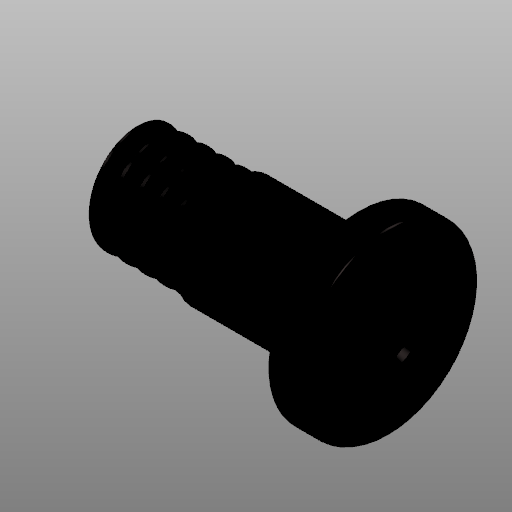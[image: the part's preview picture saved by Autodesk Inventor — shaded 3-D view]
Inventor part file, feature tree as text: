
AUTODESK INVENTOR PART (.ipt)
format: ipt  version: 2021 (Build 250183000, 183)  size: 366,080 bytes
history: native  units: in
note: dims shown in document units (in); Inventor stores cm internally (conversion verified against a paired STEP export)
features: other x3, sketch x2, extrude x2, imported_body x1
ambient origin geometry x8: Origin, YZ Plane, XZ Plane, XY Plane, X Axis, Y Axis, Z Axis, Center Point
bodies: Body1 (feature_tree), Body2 (feature_tree), Body3 (feature_tree)
feature tree (8):
  parser-record x1  (decoder bookkeeping rows leaked as tree rows — omitted from the tree; the rows remain in map.json)
  imported_body  "Base1"
  sketch  "Sketch1"  dims[d0=0.001in d1=0.001in d2=0.0in]
  other  "Srf1"
  sketch  "Sketch2"  dims[d4=0.001in d5=0.001in d6=0.0in]
  other  "Srf2"
  extrude  "ExtrusionSrf1"  Depth=0.001in TaperAngle=0.0deg
  extrude  "ExtrusionSrf2"  Depth=0.001in TaperAngle=0.0deg
